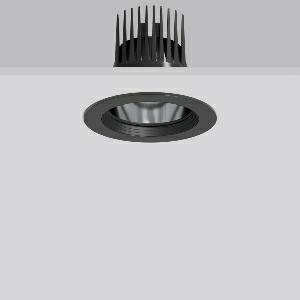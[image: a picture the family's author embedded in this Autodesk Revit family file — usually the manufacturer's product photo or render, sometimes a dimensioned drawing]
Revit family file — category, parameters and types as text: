
# Revit family: heledon_maxi_e_901766_003_2_76_c66e
name_source: partatom
category: Lighting Fixtures
units: mm (PartAtom-declared; Revit-internal decimal feet)

## family parameters
Cut with Voids When Loaded = No
Host = Face
Light Source = No
Part Type = Normal
Room Calculation Point = No
Round Connector Dimension = Use Diameter
Shared = No

## types (1)
- HELEDON maxi E (1 x LED Modul 927, 3950 lm, 2700)
    Apparent Load = 35 VA
    Approval mark = CE
    CIE Flux Codes = 97 100 100 100 100
    Color Rendering = 92
    Color Temperature = 2700
    Default Elevation = 1800 mm
    Description = Series: HELEDON maxi
Round recessed downlight. Housing: die-cast aluminium, powder-coated. Black plastic ring and recessed LED to prevent glare from the side. Optical assembly with reflector made of MIRO-Silver with 98% total light reflection for outstanding efficiency - can be changed without tools. Best colour rendering index Ra>90. Suitable for Recessed ceiling mounting. Installation without tools thanks to spring fastening system. Including separate LED converter with connecting cable 600 mm.High quality converter without flickering and stroboscopic effect. Through-wiring box (5 pole) available as accessory. The following accessories can be mounted without use of tools: interchangeable lenses, decorative glasses, honeycomb louvre, clear and frosted diffusers, white interchangeable plastic ring. 
Colour: deep black, matt (RAL 9005)
Diameter: 162 mm
Height: 3 mm
Cut-out diameter: 152 mm
Recess height: 200 mm
Luminaire: recess height: 135 mm
Lamp: LED
Socket: without socket
Colour temperature: 2700K
Colour rendering index (CRI): 92
System power: 35 W
Rated luminous flux: 3950 lm
Luminous efficiency: 113 lm/W
Control gear: Converter, dimmable, DALI
Protection class: II
Type of protection: IP 20
    Height = 0 mm  [stored 0 ft]
    Lamp = 1 x LED Modul 927
    Lamp Light Flux = 3950 lm
    Lamp count = 1
    Length = 162 mm
    Lifetime = 50000 h
    Luminous efficacy = 113 lm/W
    Manufacturer = RZB
    ModVariant = No
    Model = 901766.003.2.76
    Mounting Place = Ceiling
    Mounting Type = Recessed
    Number of Poles = 1
    OnlyDefault = Yes
    Power Factor = 1
    Product Name = HELEDON maxi E
    Product group = Recessed downlights
    ProductGroupID = 402
    Protection Class = Protection class II
    Protection Degree = IP 20
    RLX_Detail_Level = 1
    RLX_Emergency_Light_Flux = 0 lm
    RLX_Emergency_Type = 0
    RLX_Emergency_Type_DB = No
    RlxData = <blob elided: 122689 chars, md5=2316ca50>
    Socket = socket
    Standby Power = 0 W
    System Light Flux = 3950 lm
    System Power = 35 W
    Type Comments = Product without accessories
    Type Image = 901662.003.jpg
    URL = http://relux.com
    VarID = ---
    Voltage = 230 V
    Voltage Range = 220-240 V
    Weight = 0.00 kg
    Width = 0 mm  [stored 0 ft]

note: [stored X ft] marks values corroborated as IEEE doubles in the binary element streams (Revit-internal decimal feet)

## geometry (parser evidence)
native form markers: Blend x4, Sweep x12
no freeform markers — native parametric forms only
